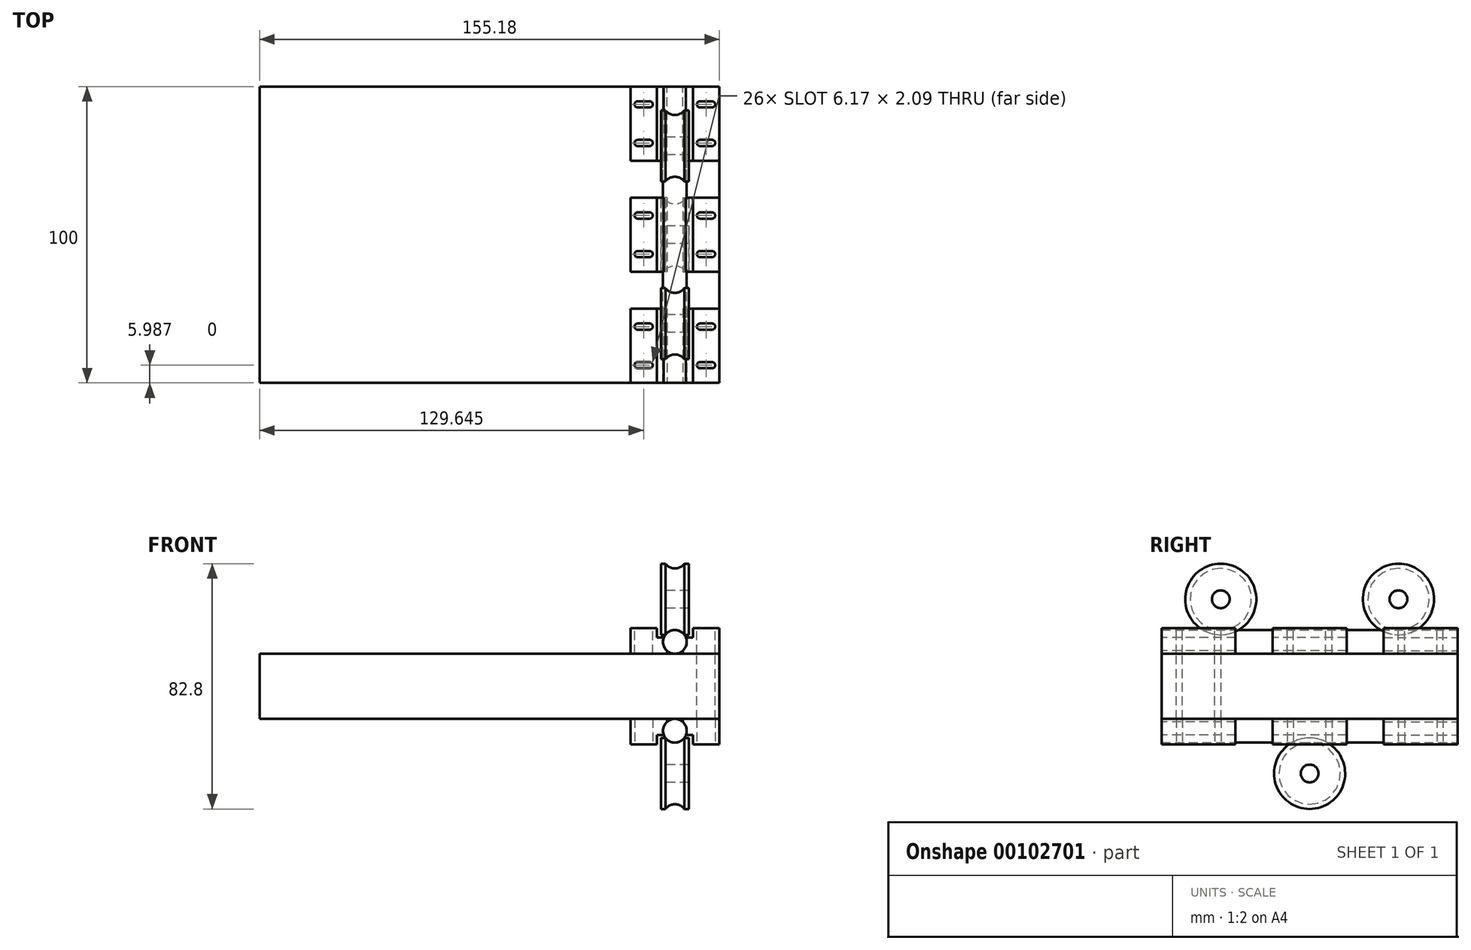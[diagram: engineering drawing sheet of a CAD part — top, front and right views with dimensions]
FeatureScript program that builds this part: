
annotation { "Feature Type Name" : "Feature", "Feature Type Description" : "" }
export const myFeature = defineFeature(function(context is Context, id is Id, definition is map)
    precondition{}
    {
        {
            var Q0;
            Q0=qCreatedBy(makeId("Front.planeOp"),FACE);
            var sketch = newSketch(context, id + "F0", { "sketchPlane" : qUnion([Q0])});
            skCircle(sketch, "E0", {"center": v(0, 0) * mm, "radius": 4 * mm});
            skLineSegment(sketch, "E1", {"start": v(3.2, 2.4) * mm, "end": v(4.7, 2.4) * mm});
            skLineSegment(sketch, "E2", {"start": v(4, 8.7) * mm, "end": v(4, -8.8) * mm, "construction": true});
            skLineSegment(sketch, "E3", {"start": v(-9.41, 14.4) * mm, "end": v(10.74, 14.4) * mm, "construction": true});
            skLineSegment(sketch, "E4", {"start": v(4.7, 2.4) * mm, "end": v(4.7, 11.4) * mm});
            skLineSegment(sketch, "E5", {"start": v(4.7, 11.4) * mm, "end": v(0, 11.4) * mm});
            skLineSegment(sketch, "E6.MirrorCS", {"start": v(-4.7, 11.4) * mm, "end": v(0, 11.4) * mm});
            skLineSegment(sketch, "E7.MirrorCS", {"start": v(-4.7, 2.4) * mm, "end": v(-4.7, 11.4) * mm});
            skLineSegment(sketch, "E8.MirrorCS", {"start": v(-3.2, 2.4) * mm, "end": v(-4.7, 2.4) * mm});
            skLineSegment(sketch, "E9", {"start": v(0, -4) * mm, "end": v(15, -4) * mm});
            skLineSegment(sketch, "E10", {"start": v(15, -4) * mm, "end": v(15, -26) * mm});
            skLineSegment(sketch, "E11", {"start": v(15, -26) * mm, "end": v(0, -26) * mm});
            skLineSegment(sketch, "E12.MirrorCS", {"start": v(0, -4) * mm, "end": v(-140.18, -4) * mm});
            skLineSegment(sketch, "E13.MirrorCS", {"start": v(-140.18, -4) * mm, "end": v(-140.18, -26) * mm});
            skLineSegment(sketch, "E14.MirrorCS", {"start": v(-140.18, -26) * mm, "end": v(0, -26) * mm});
            skSolve(sketch);
        }
        {
            var Q0;
            {var subQ0=sQuery(id+"F0.wireOp",EDGE,"E0");var subQ1=makeQuery(id+"F0.imprint","INTERSECT",VERTEX,{"derivedFrom":[subQ0,sQuery(id+"F0.wireOp",EDGE,"E1")]});Q0=makeQuery(id+"F0.imprint","IMPRINT",FACE,{"disambiguationData":[TD([[makeQuery(id+"F0.imprint","IMPRINT",EDGE,{"disambiguationData":[TD([[subQ1,-1.0]])],"derivedFrom":subQ0}),1.0]])]});}
            extrude(context, id + "F1", {"entities" : qUnion([Q0]), "endBound" : BoundingType.SYMMETRIC, "depth" : 100 * mm});
        }
        {
            var Q0;
            {var subQ0=sQuery(id+"F0.wireOp",EDGE,"E1");Q0=makeQuery(id+"F0.imprint","IMPRINT",FACE,{"disambiguationData":[TD([[makeQuery(id+"F0.imprint","IMPRINT",EDGE,{"derivedFrom":subQ0}),1.0]])]});}
            var Q1;
            Q1=sQuery(id+"F0.wireOp",EDGE,"E3");
            revolve(context, id + "F2", {"operationType" : NewBodyOperationType.ADD, "entities" : qUnion([Q0]), "axis" : qUnion([Q1]), "revolveType" : RevolveType.FULL});
        }
        {
            var Q0;
            Q0=makeQuery(id+"F0.imprint","IMPRINT",FACE,{"disambiguationData":[TD([[makeQuery(id+"F0.imprint","IMPRINT",EDGE,{"derivedFrom":sQuery(id+"F0.wireOp",EDGE,"E9")}),-1.0]])]});
            extrude(context, id + "F3", {"entities" : qUnion([Q0]), "operationType" : NewBodyOperationType.ADD, "endBound" : BoundingType.SYMMETRIC, "depth" : 100 * mm});
        }
        {
            var Q0;
            Q0=makeQuery(id+"F3.opExtrude","CAP_FACE",FACE,{"disambiguationData":[OSD([sQuery(id+"F0.wireOp",EDGE,"E9"),sQuery(id+"F0.wireOp",EDGE,"E10"),sQuery(id+"F0.wireOp",EDGE,"E11"),sQuery(id+"F0.wireOp",EDGE,"E12.MirrorCS"),sQuery(id+"F0.wireOp",EDGE,"E13.MirrorCS"),sQuery(id+"F0.wireOp",EDGE,"E14.MirrorCS")])],"isStart":false});
            var sketch = newSketch(context, id + "F4", { "sketchPlane" : qUnion([Q0])});
            skCircle(sketch, "E15.0", {"center": v(0, 0) * mm, "radius": 4 * mm});
            skLineSegment(sketch, "E16.0", {"start": v(-140.18, -4) * mm, "end": v(15, -4) * mm});
            skLineSegment(sketch, "E17", {"start": v(3.75, 1.4) * mm, "end": v(6.07, 1.4) * mm});
            skLineSegment(sketch, "E18", {"start": v(4.7, 2.4) * mm, "end": v(3.2, 2.4) * mm, "construction": true});
            skLineSegment(sketch, "E19", {"start": v(6.07, 1.4) * mm, "end": v(6.07, 4.64) * mm});
            skLineSegment(sketch, "E20", {"start": v(6.07, 4.64) * mm, "end": v(15, 4.64) * mm});
            skLineSegment(sketch, "E21", {"start": v(15, 4.64) * mm, "end": v(15, -4) * mm});
            skLineSegment(sketch, "E22", {"start": v(2.7, -2.96) * mm, "end": v(2.7, -4) * mm});
            skSolve(sketch);
        }
        {
            var Q0;
            {var subQ0=sQuery(id+"F4.wireOp",EDGE,"E17");Q0=makeQuery(id+"F4.imprint","IMPRINT",FACE,{"disambiguationData":[TD([[makeQuery(id+"F4.imprint","IMPRINT",EDGE,{"derivedFrom":subQ0}),-1.0]])]});}
            extrude(context, id + "F5", {"entities" : qUnion([Q0]), "oppositeDirection" : true, "depth" : 25 * mm});
        }
        {
            var Q0;
            Q0=makeQuery(id+"F5.opExtrude","SWEPT_FACE",FACE,{"disambiguationData":[OSD([sQuery(id+"F4.wireOp",EDGE,"E20")])]});
            var sketch = newSketch(context, id + "F6", { "sketchPlane" : qUnion([Q0])});
            skLineSegment(sketch, "E23", {"start": v(10.53, -25) * mm, "end": v(10.53, -50) * mm, "construction": true});
            skLineSegment(sketch, "E24", {"start": v(6.07, -37.5) * mm, "end": v(15, -37.5) * mm, "construction": true});
            skLineSegment(sketch, "E25", {"start": v(10.53, -42.97) * mm, "end": v(8.5, -42.97) * mm});
            skLineSegment(sketch, "E26", {"start": v(10.53, -45.06) * mm, "end": v(8.5, -45.06) * mm});
            skArc(sketch, "E27", {"start": v(8.5, -42.97) * mm, "mid": v(7.45, -44.01) * mm, "end": v(8.5, -45.06) * mm});
            skLineSegment(sketch, "E28.MirrorCS", {"start": v(10.53, -42.97) * mm, "end": v(12.58, -42.97) * mm});
            skArc(sketch, "E29.MirrorCS", {"start": v(12.58, -42.97) * mm, "mid": v(13.62, -44.01) * mm, "end": v(12.58, -45.06) * mm});
            skLineSegment(sketch, "E30.MirrorCS", {"start": v(10.53, -45.06) * mm, "end": v(12.58, -45.06) * mm});
            skLineSegment(sketch, "E31.MirrorCS", {"start": v(10.53, -32.03) * mm, "end": v(8.5, -32.03) * mm});
            skArc(sketch, "E32.MirrorCS", {"start": v(8.5, -32.03) * mm, "mid": v(7.45, -30.99) * mm, "end": v(8.5, -29.94) * mm});
            skLineSegment(sketch, "E33.MirrorCS", {"start": v(10.53, -29.94) * mm, "end": v(8.5, -29.94) * mm});
            skLineSegment(sketch, "E34.MirrorCS", {"start": v(10.53, -29.94) * mm, "end": v(12.58, -29.94) * mm});
            skArc(sketch, "E35.MirrorCS", {"start": v(12.58, -32.03) * mm, "mid": v(13.62, -30.99) * mm, "end": v(12.58, -29.94) * mm});
            skLineSegment(sketch, "E36.MirrorCS", {"start": v(10.53, -32.03) * mm, "end": v(12.58, -32.03) * mm});
            skSolve(sketch);
        }
        {
            var Q0;
            Q0 = qSketchRegion(id + "F6", true);
            extrude(context, id + "F7", {"entities" : qUnion([Q0]), "operationType" : NewBodyOperationType.REMOVE, "endBound" : BoundingType.THROUGH_ALL, "oppositeDirection" : true, "depth" : 25 * mm});
        }
        {
            var Q0;
            Q0=makeQuery(id+"F5.opExtrude","SWEPT_BODY",BODY,{"disambiguationData":[OSD([sQuery(id+"F4.wireOp",EDGE,"E15.0"),sQuery(id+"F4.wireOp",EDGE,"E16.0"),sQuery(id+"F4.wireOp",EDGE,"E17"),sQuery(id+"F4.wireOp",EDGE,"E19"),sQuery(id+"F4.wireOp",EDGE,"E20"),sQuery(id+"F4.wireOp",EDGE,"E21"),sQuery(id+"F4.wireOp",EDGE,"E22")])]});
            var Q1;
            Q1=qCreatedBy(makeId("Right.planeOp"),FACE);
            mirror(context, id + "F8", {"entities" : qUnion([Q0]), "mirrorPlane" : qUnion([Q1])});
        }
        {
            var Q0;
            Q0=makeQuery(id+"F5.opExtrude","SWEPT_BODY",BODY,{"disambiguationData":[OSD([sQuery(id+"F4.wireOp",EDGE,"E15.0"),sQuery(id+"F4.wireOp",EDGE,"E16.0"),sQuery(id+"F4.wireOp",EDGE,"E17"),sQuery(id+"F4.wireOp",EDGE,"E19"),sQuery(id+"F4.wireOp",EDGE,"E20"),sQuery(id+"F4.wireOp",EDGE,"E21"),sQuery(id+"F4.wireOp",EDGE,"E22")])]});
            var Q1;
            Q1=makeQuery(id+"F8.opPattern","COPY",BODY,{"derivedFrom":makeQuery(id+"F5.opExtrude","SWEPT_BODY",BODY,{"disambiguationData":[OSD([sQuery(id+"F4.wireOp",EDGE,"E15.0"),sQuery(id+"F4.wireOp",EDGE,"E16.0"),sQuery(id+"F4.wireOp",EDGE,"E17"),sQuery(id+"F4.wireOp",EDGE,"E19"),sQuery(id+"F4.wireOp",EDGE,"E20"),sQuery(id+"F4.wireOp",EDGE,"E21"),sQuery(id+"F4.wireOp",EDGE,"E22")])]}),"instanceName":"1"});
            var Q2;
            Q2=qCreatedBy(makeId("Front.planeOp"),FACE);
            mirror(context, id + "F9", {"entities" : qUnion([Q0, Q1]), "mirrorPlane" : qUnion([Q2])});
        }
        {
            var Q0;
            Q0=qCreatedBy(makeId("Top.planeOp"),FACE);
            cPlane(context, id + "F10", {"entities" : qUnion([Q0]), "cplaneType" : CPlaneType.OFFSET, "offset" : 15 * mm, "oppositeDirection" : true, "width" : 150 * mm, "height" : 150 * mm});
        }
        {
            var Q0;
            Q0=makeQuery(id+"F2.opRevolve","SWEPT_BODY",BODY,{"disambiguationData":[OSD([sQuery(id+"F0.wireOp",EDGE,"E0"),sQuery(id+"F0.wireOp",EDGE,"E1"),sQuery(id+"F0.wireOp",EDGE,"E4"),sQuery(id+"F0.wireOp",EDGE,"E5"),sQuery(id+"F0.wireOp",EDGE,"E6.MirrorCS"),sQuery(id+"F0.wireOp",EDGE,"E7.MirrorCS"),sQuery(id+"F0.wireOp",EDGE,"E8.MirrorCS")])]});
            var Q1;
            Q1=makeQuery(id+"F1.opExtrude","SWEPT_BODY",BODY,{"disambiguationData":[OSD([sQuery(id+"F0.wireOp",EDGE,"E0")])]});
            var Q2;
            Q2=makeQuery(id+"F8.opPattern","COPY",BODY,{"derivedFrom":makeQuery(id+"F5.opExtrude","SWEPT_BODY",BODY,{"disambiguationData":[OSD([sQuery(id+"F4.wireOp",EDGE,"E15.0"),sQuery(id+"F4.wireOp",EDGE,"E16.0"),sQuery(id+"F4.wireOp",EDGE,"E17"),sQuery(id+"F4.wireOp",EDGE,"E19"),sQuery(id+"F4.wireOp",EDGE,"E20"),sQuery(id+"F4.wireOp",EDGE,"E21"),sQuery(id+"F4.wireOp",EDGE,"E22")])]}),"instanceName":"1"});
            var Q3;
            Q3=makeQuery(id+"F5.opExtrude","SWEPT_BODY",BODY,{"disambiguationData":[OSD([sQuery(id+"F4.wireOp",EDGE,"E15.0"),sQuery(id+"F4.wireOp",EDGE,"E16.0"),sQuery(id+"F4.wireOp",EDGE,"E17"),sQuery(id+"F4.wireOp",EDGE,"E19"),sQuery(id+"F4.wireOp",EDGE,"E20"),sQuery(id+"F4.wireOp",EDGE,"E21"),sQuery(id+"F4.wireOp",EDGE,"E22")])]});
            var Q4;
            Q4=makeQuery(id+"F9.opPattern","COPY",BODY,{"derivedFrom":makeQuery(id+"F5.opExtrude","SWEPT_BODY",BODY,{"disambiguationData":[OSD([sQuery(id+"F4.wireOp",EDGE,"E15.0"),sQuery(id+"F4.wireOp",EDGE,"E16.0"),sQuery(id+"F4.wireOp",EDGE,"E17"),sQuery(id+"F4.wireOp",EDGE,"E19"),sQuery(id+"F4.wireOp",EDGE,"E20"),sQuery(id+"F4.wireOp",EDGE,"E21"),sQuery(id+"F4.wireOp",EDGE,"E22")])]}),"instanceName":"1"});
            var Q5;
            Q5=makeQuery(id+"F9.opPattern","COPY",BODY,{"derivedFrom":makeQuery(id+"F8.opPattern","COPY",BODY,{"derivedFrom":makeQuery(id+"F5.opExtrude","SWEPT_BODY",BODY,{"disambiguationData":[OSD([sQuery(id+"F4.wireOp",EDGE,"E15.0"),sQuery(id+"F4.wireOp",EDGE,"E16.0"),sQuery(id+"F4.wireOp",EDGE,"E17"),sQuery(id+"F4.wireOp",EDGE,"E19"),sQuery(id+"F4.wireOp",EDGE,"E20"),sQuery(id+"F4.wireOp",EDGE,"E21"),sQuery(id+"F4.wireOp",EDGE,"E22")])]}),"instanceName":"1"}),"instanceName":"1"});
            var Q6;
            Q6=qCreatedBy(id+"F10.planeOp",FACE);
            mirror(context, id + "F11", {"entities" : qUnion([Q0, Q1, Q2, Q3, Q4, Q5]), "mirrorPlane" : qUnion([Q6])});
        }
        {
            var Q0;
            Q0=makeQuery(id+"F2.opRevolve","SWEPT_BODY",BODY,{"disambiguationData":[OSD([sQuery(id+"F0.wireOp",EDGE,"E0"),sQuery(id+"F0.wireOp",EDGE,"E1"),sQuery(id+"F0.wireOp",EDGE,"E4"),sQuery(id+"F0.wireOp",EDGE,"E5"),sQuery(id+"F0.wireOp",EDGE,"E6.MirrorCS"),sQuery(id+"F0.wireOp",EDGE,"E7.MirrorCS"),sQuery(id+"F0.wireOp",EDGE,"E8.MirrorCS")])]});
            var Q1;
            Q1=makeQuery(id+"F5.opExtrude","SWEPT_EDGE",EDGE,{"disambiguationData":[OSD([sQuery(id+"F4.wireOp",EDGE,"E20"),sQuery(id+"F4.wireOp",EDGE,"E21")])]});
            transform(context, id + "F12", {"entities" : qUnion([Q0]), "transformType" : TransformType.TRANSLATION_DISTANCE, "transformDirection" : qUnion([Q1]), "distance" : 30 * mm, "makeCopy" : false});
        }
        {
            var Q0;
            Q0=makeQuery(id+"F2.opRevolve","SWEPT_BODY",BODY,{"disambiguationData":[OSD([sQuery(id+"F0.wireOp",EDGE,"E0"),sQuery(id+"F0.wireOp",EDGE,"E1"),sQuery(id+"F0.wireOp",EDGE,"E4"),sQuery(id+"F0.wireOp",EDGE,"E5"),sQuery(id+"F0.wireOp",EDGE,"E6.MirrorCS"),sQuery(id+"F0.wireOp",EDGE,"E7.MirrorCS"),sQuery(id+"F0.wireOp",EDGE,"E8.MirrorCS")])]});
            var Q1;
            Q1=qCreatedBy(makeId("Front.planeOp"),FACE);
            mirror(context, id + "F13", {"operationType" : NewBodyOperationType.ADD, "entities" : qUnion([Q0]), "mirrorPlane" : qUnion([Q1])});
        }
        {
            var Q0;
            Q0=makeQuery(id+"F5.opExtrude","SWEPT_BODY",BODY,{"disambiguationData":[OSD([sQuery(id+"F4.wireOp",EDGE,"E15.0"),sQuery(id+"F4.wireOp",EDGE,"E16.0"),sQuery(id+"F4.wireOp",EDGE,"E17"),sQuery(id+"F4.wireOp",EDGE,"E19"),sQuery(id+"F4.wireOp",EDGE,"E20"),sQuery(id+"F4.wireOp",EDGE,"E21"),sQuery(id+"F4.wireOp",EDGE,"E22")])]});
            var Q1;
            Q1=makeQuery(id+"F8.opPattern","COPY",BODY,{"derivedFrom":makeQuery(id+"F5.opExtrude","SWEPT_BODY",BODY,{"disambiguationData":[OSD([sQuery(id+"F4.wireOp",EDGE,"E15.0"),sQuery(id+"F4.wireOp",EDGE,"E16.0"),sQuery(id+"F4.wireOp",EDGE,"E17"),sQuery(id+"F4.wireOp",EDGE,"E19"),sQuery(id+"F4.wireOp",EDGE,"E20"),sQuery(id+"F4.wireOp",EDGE,"E21"),sQuery(id+"F4.wireOp",EDGE,"E22")])]}),"instanceName":"1"});
            var Q2;
            Q2=makeQuery(id+"F11.opPattern","COPY",BODY,{"derivedFrom":makeQuery(id+"F5.opExtrude","SWEPT_BODY",BODY,{"disambiguationData":[OSD([sQuery(id+"F4.wireOp",EDGE,"E15.0"),sQuery(id+"F4.wireOp",EDGE,"E16.0"),sQuery(id+"F4.wireOp",EDGE,"E17"),sQuery(id+"F4.wireOp",EDGE,"E19"),sQuery(id+"F4.wireOp",EDGE,"E20"),sQuery(id+"F4.wireOp",EDGE,"E21"),sQuery(id+"F4.wireOp",EDGE,"E22")])]}),"instanceName":"1"});
            var Q3;
            Q3=makeQuery(id+"F11.opPattern","COPY",BODY,{"derivedFrom":makeQuery(id+"F8.opPattern","COPY",BODY,{"derivedFrom":makeQuery(id+"F5.opExtrude","SWEPT_BODY",BODY,{"disambiguationData":[OSD([sQuery(id+"F4.wireOp",EDGE,"E15.0"),sQuery(id+"F4.wireOp",EDGE,"E16.0"),sQuery(id+"F4.wireOp",EDGE,"E17"),sQuery(id+"F4.wireOp",EDGE,"E19"),sQuery(id+"F4.wireOp",EDGE,"E20"),sQuery(id+"F4.wireOp",EDGE,"E21"),sQuery(id+"F4.wireOp",EDGE,"E22")])]}),"instanceName":"1"}),"instanceName":"1"});
            var Q4;
            Q4=makeQuery(id+"F3.opExtrude","SWEPT_EDGE",EDGE,{"disambiguationData":[OSD([sQuery(id+"F0.wireOp",EDGE,"E9"),sQuery(id+"F0.wireOp",EDGE,"E10")])]});
            transform(context, id + "F14", {"entities" : qUnion([Q0, Q1, Q2, Q3]), "transformType" : TransformType.TRANSLATION_DISTANCE, "transformDirection" : qUnion([Q4]), "distance" : 37.5 * mm, "makeCopy" : true});
        }
    });
